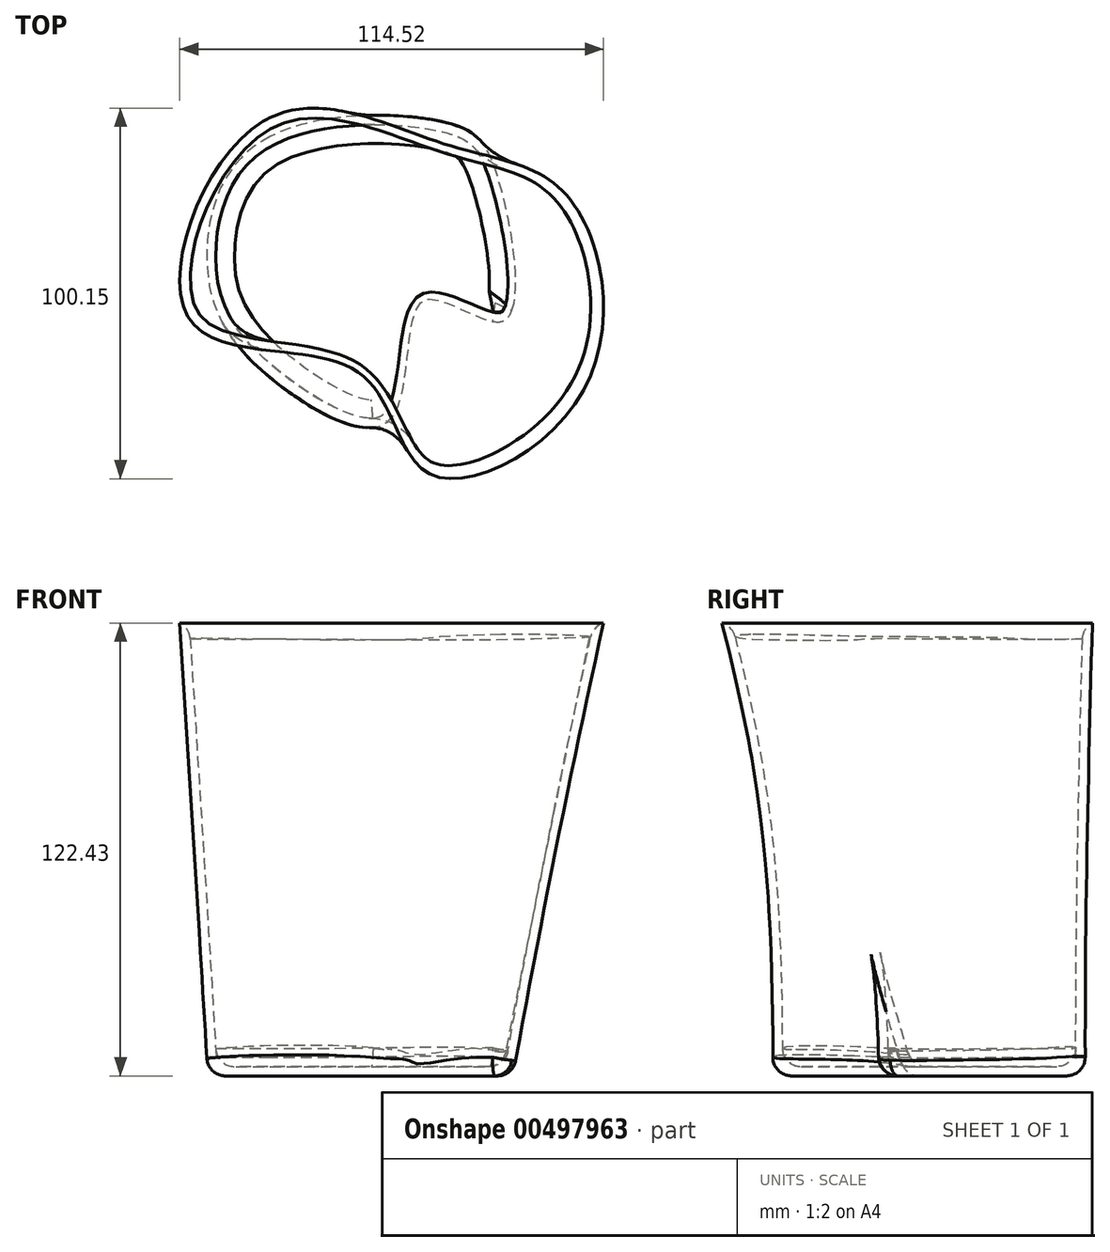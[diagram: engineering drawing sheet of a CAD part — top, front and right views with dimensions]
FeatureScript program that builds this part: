
annotation { "Feature Type Name" : "Feature", "Feature Type Description" : "" }
export const myFeature = defineFeature(function(context is Context, id is Id, definition is map)
    precondition{}
    {
        {
            var Q0;
            Q0=qCreatedBy(makeId("Top.planeOp"),FACE);
            var sketch = newSketch(context, id + "F0", { "sketchPlane" : qUnion([Q0])});
            skFitSpline(sketch, "E0", {"points": [v(33.39, 39.43) * mm, v(21.3, 53.53) * mm, v(-30.22, 48.06) * mm, v(-44.32, 17.56) * mm, v(-31.66, -12.38) * mm, v(4.6, -26.48) * mm, v(13.24, 6.62) * mm, v(34.54, 0) * mm, v(33.39, 39.43) * mm]});
            skSolve(sketch);
        }
        {
            var Q0;
            Q0=qCreatedBy(makeId("Top.planeOp"),FACE);
            cPlane(context, id + "F1", {"entities" : qUnion([Q0]), "cplaneType" : CPlaneType.OFFSET, "offset" : 122.43 * mm, "width" : 152.4 * mm, "height" : 152.4 * mm});
        }
        {
            var Q0;
            Q0=qCreatedBy(id+"F1.planeOp",FACE);
            var sketch = newSketch(context, id + "F2", { "sketchPlane" : qUnion([Q0])});
            skFitSpline(sketch, "E1", {"points": [v(-29.48, 53.84) * mm, v(-48.97, 0) * mm, v(-3.92, -13.74) * mm, v(15.5, -41.33) * mm, v(57.18, -18.78) * mm, v(52.67, 33.9) * mm, v(19.97, 47.7) * mm, v(-29.48, 53.84) * mm]});
            skSolve(sketch);
        }
        {
            var Q0;
            Q0=makeQuery(id+"F2.imprint","IMPRINT",FACE,{"disambiguationData":[TD([[makeQuery(id+"F2.imprint","IMPRINT",EDGE,{"derivedFrom":sQuery(id+"F2.wireOp",EDGE,"E1")}),1.0]])]});
            var Q1;
            Q1=makeQuery(id+"F0.imprint","IMPRINT",FACE,{"disambiguationData":[TD([[makeQuery(id+"F0.imprint","IMPRINT",EDGE,{"derivedFrom":sQuery(id+"F0.wireOp",EDGE,"E0")}),1.0]])]});
            loft(context, id + "F3", {"sheetProfilesArray" : [{ "sheetProfileEntities" : qUnion([Q0]) }, { "sheetProfileEntities" : qUnion([Q1]) }]});
        }
        {
            var Q0;
            Q0=makeQuery(id+"F3.opLoft","CAP_FACE",FACE,{"disambiguationData":[OSD([makeQuery(id+"F2.imprint","IMPRINT",FACE,{"disambiguationData":[TD([[makeQuery(id+"F2.imprint","IMPRINT",EDGE,{"derivedFrom":sQuery(id+"F2.wireOp",EDGE,"E1")}),1.0]])]})])],"isStart":true});
            shell(context, id + "F4", {"entities" : qUnion([Q0]), "thickness" : 2.54 * mm});
        }
        {
            var Q0;
            Q0=makeQuery(id+"F4.opShell","OFFSET_EDGE",EDGE,{"disambiguationData":[OSD([sQuery(id+"F0.wireOp",EDGE,"E0"),sQuery(id+"F2.wireOp",EDGE,"E1")])]});
            var Q1;
            Q1=makeQuery(id+"F3.opLoft","MID_CAP_EDGE",EDGE,{"disambiguationData":[OSD([sQuery(id+"F0.wireOp",EDGE,"E0"),sQuery(id+"F2.wireOp",EDGE,"E1")])],"capPos":1.0});
            fillet(context, id + "F5", {"entities" : qUnion([Q0, Q1]), "radius" : 5.08 * mm, "tangentPropagation" : true, "allowEdgeOverflow" : false});
        }
    });
